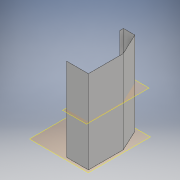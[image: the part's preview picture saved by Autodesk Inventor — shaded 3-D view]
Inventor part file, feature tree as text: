
AUTODESK INVENTOR PART (.ipt)
format: ipt  version: 2018 (Build 220112000, 112)  size: 129,536 bytes
history: native  units: mm
features: reference x5, other x3, plane x2, extrude x2, sketch x2, mirror x1
ambient origin geometry x8: Origin, YZ Plane, XZ Plane, XY Plane, X Axis, Y Axis, Z Axis, Center Point
bodies: Solid1 (feature_tree)
feature tree (15):
  plane  "Work Plane1"
  extrude  "Extrusion1"  Depth=1.6mm
  extrude  "Extrusion2"  Depth=816.6mm
  plane  "Work Plane2"
  mirror  "Mirror1"
  sketch  "Sketch1"  dims[d0=50.0mm d1=1.6mm]
  reference  "Reference1"
  reference  "Reference2"
  reference  "Reference3"
  reference  "Reference4"
  sketch  "Sketch2"  dims[d2=1.6mm d3=816.6mm d4=816.6mm d5=1198.4mm d6=0.0mm d8=1.6mm d9=0.0mm d10=1.6mm d11=0.0mm d14=1.6mm]
  reference  "Reference5"
  other  "Lathe Model 2018.iam"
  other  "Cover V3-01:a"
  other  "Cover V3:1"
